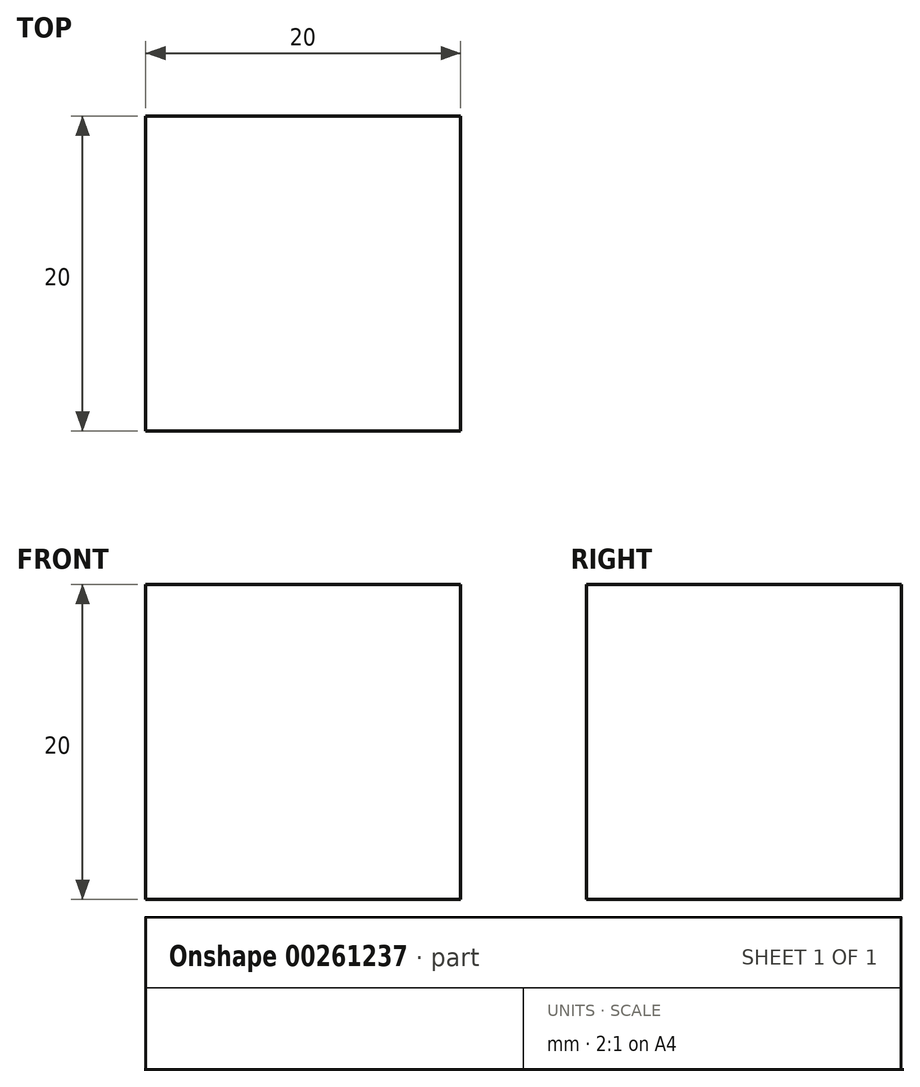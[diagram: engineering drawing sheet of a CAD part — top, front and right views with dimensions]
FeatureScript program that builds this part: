
annotation { "Feature Type Name" : "Feature", "Feature Type Description" : "" }
export const myFeature = defineFeature(function(context is Context, id is Id, definition is map)
    precondition{}
    {
        {
            var Q0;
            Q0=qCreatedBy(makeId("Right.planeOp"),FACE);
            var sketch = newSketch(context, id + "F0", { "sketchPlane" : qUnion([Q0])});
            skLineSegment(sketch, "E0.bottom", {"start": v(0, 0) * mm, "end": v(20, 0) * mm});
            skLineSegment(sketch, "E0.top", {"start": v(0, 20) * mm, "end": v(20, 20) * mm});
            skLineSegment(sketch, "E0.left", {"start": v(0, 0) * mm, "end": v(0, 20) * mm});
            skLineSegment(sketch, "E0.right", {"start": v(20, 0) * mm, "end": v(20, 20) * mm});
            skSolve(sketch);
        }
        {
            var Q0;
            Q0=makeQuery(id+"F0.imprint","IMPRINT",FACE,{"disambiguationData":[TD([[makeQuery(id+"F0.imprint","IMPRINT",EDGE,{"derivedFrom":sQuery(id+"F0.wireOp",EDGE,"E0.bottom")}),1.0]])]});
            extrude(context, id + "F1", {"entities" : qUnion([Q0]), "depth" : 20 * mm});
        }
    });
